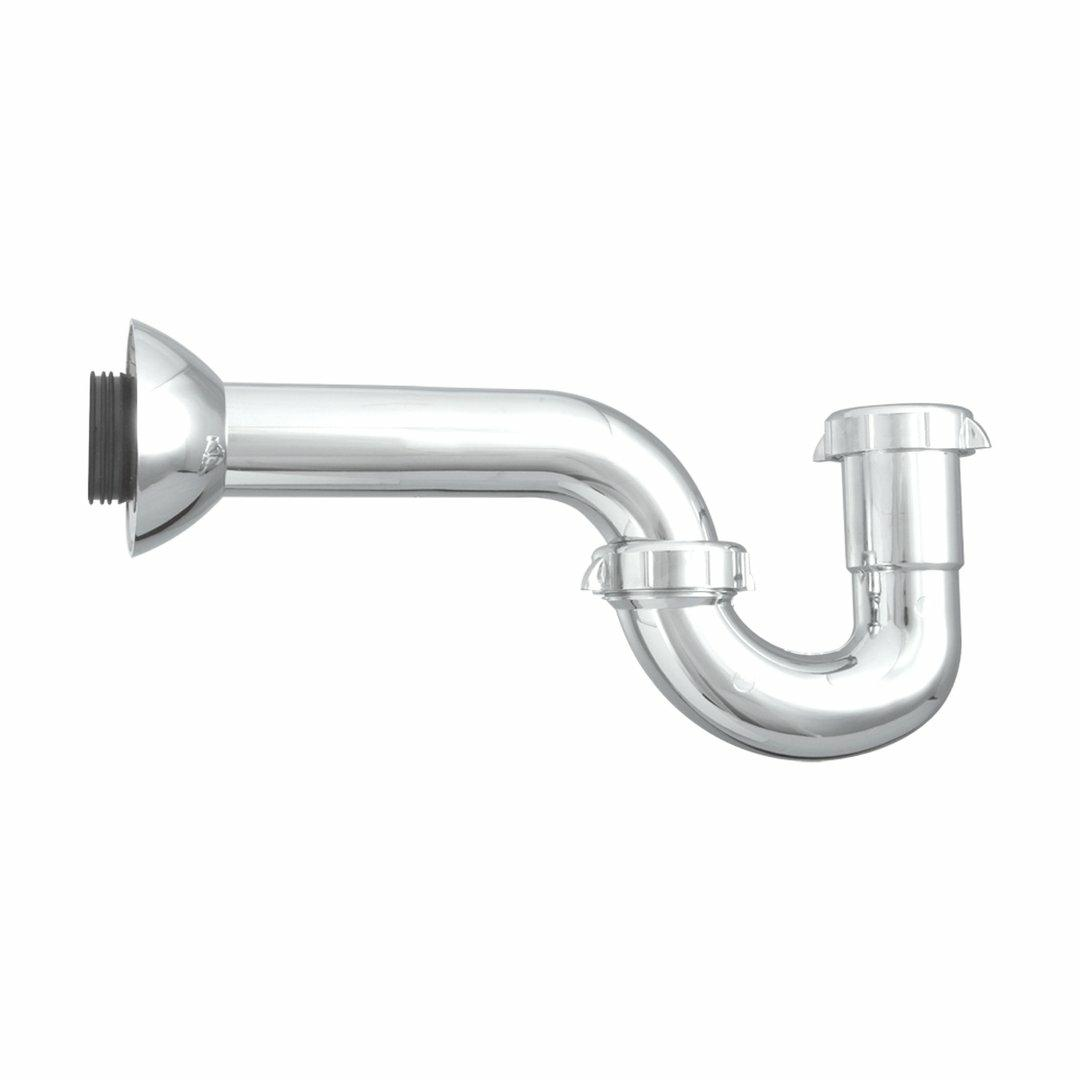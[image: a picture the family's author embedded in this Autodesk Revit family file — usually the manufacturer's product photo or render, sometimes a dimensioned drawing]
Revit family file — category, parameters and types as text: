
# Revit family: BIM_M1-3063-11
name_source: partatom
category: Aparatos sanitarios
units: mm (PartAtom-declared; Revit-internal decimal feet)

## family parameters
Activar corte en vistas = No
Anfitrión = Cara
Compartido = No
Corte con vacíos al cargar = No
Cota de conector redondo = Usar diámetro
Mantener orientación de anotación = No
Número OmniClass = 23.31.11.00
Punto de cálculo de habitación = No
Tipo de pieza = Normal

## types (1)
- M1-3063-11
    Acabado = Cepillado Brillante
    Alto = 185 mm  [stored 0.606955 ft]
    Ancho = 835 mm
    Conexión AC = Sí
    Conexión AF = Sí
    Conexión de residuos = No
    Conexión de ventilación = No
    Date Modified = 08-08-2025
    Descripción = Lavaplatos en acero
    Elevación por defecto = 0 mm  [stored 0 ft]
    Fabricante = Gricol
    Garantia Especifica = 5 año
    Imagen de tipo = FOTO LAVAPLATOS EN ACERO DOBLE POCETA 83,5 x 55,5 cm.jpg
    Largo = 555 mm
    Link Ficha Tecnica = https://infotecnica.gricol.com
    Material = Acero inoxidable
    Materiales del producto = Acero Inoxidable
    Modelo = M1-3063-11
    Nota clave = Perforación para instalar grifería monomando
    Peso = 4.75 kg
    Product Name = Lavaplatos De Empotrar Doble Poceta 84 X 56 Cm Con Complementos
    Resistencia a Corrosión = Si
    Sitio web = https://www.gricol.com
    Tipo de Uso = Residencial
    URL = https://www.gricol.com

note: [stored X ft] marks values corroborated as IEEE doubles in the binary element streams (Revit-internal decimal feet)

## geometry (parser evidence)
native form markers: Blend x2, Sweep x14
no freeform markers — native parametric forms only
